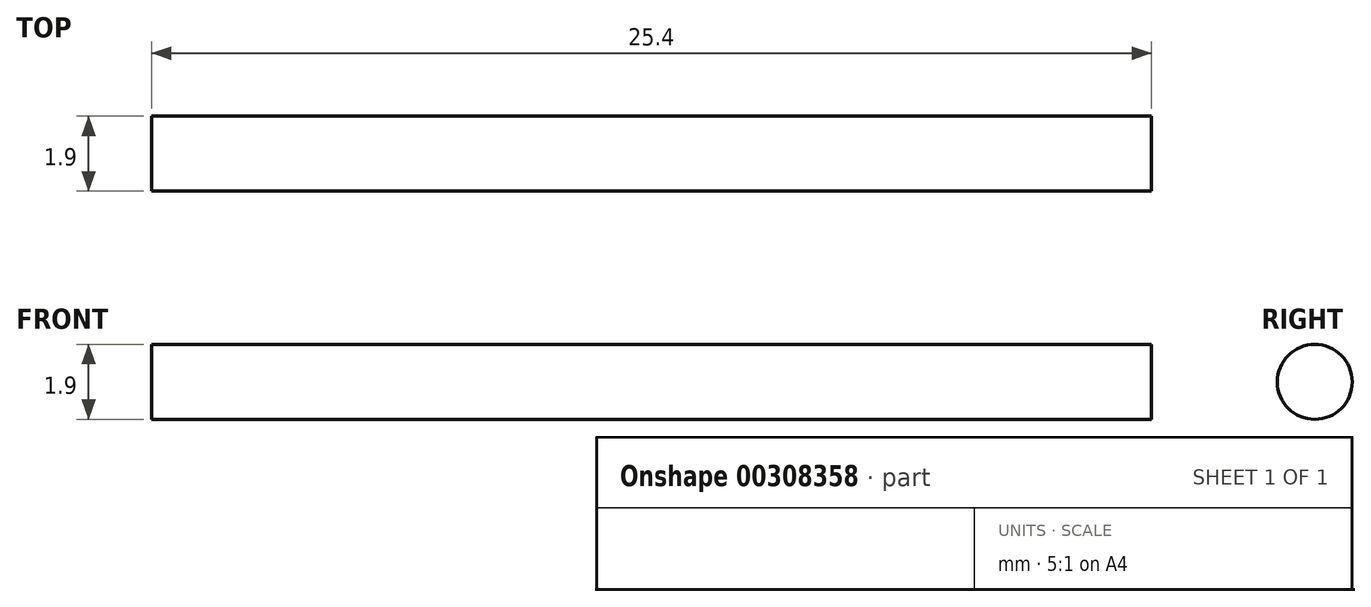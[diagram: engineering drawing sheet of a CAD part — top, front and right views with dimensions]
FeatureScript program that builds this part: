
annotation { "Feature Type Name" : "Feature", "Feature Type Description" : "" }
export const myFeature = defineFeature(function(context is Context, id is Id, definition is map)
    precondition{}
    {
        {
            var Q0;
            Q0=qCreatedBy(makeId("Right.planeOp"),FACE);
            var sketch = newSketch(context, id + "F0", { "sketchPlane" : qUnion([Q0])});
            skCircle(sketch, "E0", {"center": v(0, 0) * mm, "radius": 0.95 * mm});
            skSolve(sketch);
        }
        {
            var Q0;
            Q0=qSketchRegion(id+"F0",true);
            extrude(context, id + "F1", {"entities" : qUnion([Q0]), "depth" : 25.4 * mm});
        }
    });
